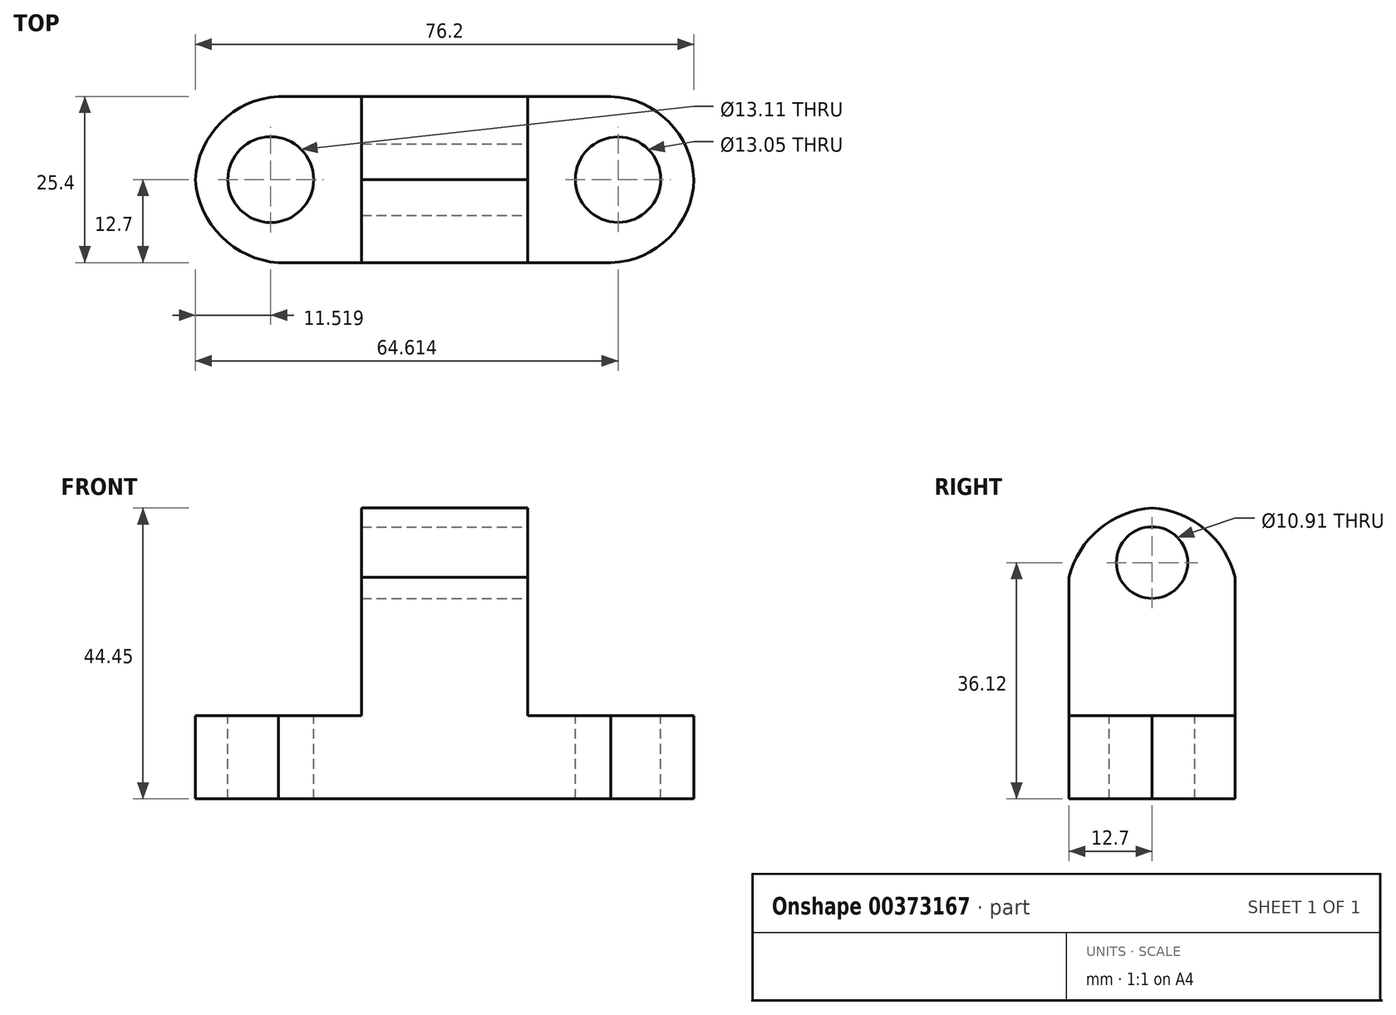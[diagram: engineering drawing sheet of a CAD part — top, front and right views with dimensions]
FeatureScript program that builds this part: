
annotation { "Feature Type Name" : "Feature", "Feature Type Description" : "" }
export const myFeature = defineFeature(function(context is Context, id is Id, definition is map)
    precondition{}
    {
        {
            var Q0;
            Q0=qCreatedBy(makeId("Front.planeOp"),FACE);
            var sketch = newSketch(context, id + "F0", { "sketchPlane" : qUnion([Q0])});
            skLineSegment(sketch, "E0", {"start": v(-13.94, 0) * mm, "end": v(-13.94, 12.7) * mm});
            skLineSegment(sketch, "E1", {"start": v(-13.94, 12.7) * mm, "end": v(11.46, 12.7) * mm});
            skLineSegment(sketch, "E2", {"start": v(11.46, 12.7) * mm, "end": v(11.46, 44.45) * mm});
            skLineSegment(sketch, "E3", {"start": v(11.46, 44.45) * mm, "end": v(36.86, 44.45) * mm});
            skLineSegment(sketch, "E4", {"start": v(36.86, 44.45) * mm, "end": v(36.86, 12.7) * mm});
            skLineSegment(sketch, "E5", {"start": v(36.86, 12.7) * mm, "end": v(62.26, 12.7) * mm});
            skLineSegment(sketch, "E6", {"start": v(62.26, 12.7) * mm, "end": v(62.26, 0) * mm});
            skLineSegment(sketch, "E7", {"start": v(62.26, 0) * mm, "end": v(-13.94, 0) * mm});
            skSolve(sketch);
        }
        {
            var Q0;
            Q0=makeQuery(id+"F0.imprint","IMPRINT",FACE,{"disambiguationData":[TD([[makeQuery(id+"F0.imprint","IMPRINT",EDGE,{"derivedFrom":sQuery(id+"F0.wireOp",EDGE,"E0")}),-1.0]])]});
            extrude(context, id + "F1", {"entities" : qUnion([Q0]), "depth" : 25.4 * mm});
        }
        {
            var Q0;
            Q0=makeQuery(id+"F1.opExtrude","SWEPT_FACE",FACE,{"disambiguationData":[OSD([sQuery(id+"F0.wireOp",EDGE,"E4")])]});
            var sketch = newSketch(context, id + "F2", { "sketchPlane" : qUnion([Q0])});
            skArc(sketch, "E8", {"start": v(-12.7, 44.45) * mm, "mid": v(-20.79, 41.23) * mm, "end": v(-25.4, 33.85) * mm});
            skArc(sketch, "E9", {"start": v(0, 33.85) * mm, "mid": v(-4.62, 41.22) * mm, "end": v(-12.7, 44.45) * mm});
            skSolve(sketch);
        }
        {
            var Q0;
            {var subQ0=sQuery(id+"F2.wireOp",EDGE,"E8");Q0=makeQuery(id+"F2.imprint","IMPRINT",FACE,{"disambiguationData":[TD([[makeQuery(id+"F2.imprint","IMPRINT",EDGE,{"derivedFrom":subQ0}),-1.0]])]});}
            var Q1;
            {var subQ0=sQuery(id+"F2.wireOp",EDGE,"E9");Q1=makeQuery(id+"F2.imprint","IMPRINT",FACE,{"disambiguationData":[TD([[makeQuery(id+"F2.imprint","IMPRINT",EDGE,{"derivedFrom":subQ0}),-1.0]])]});}
            extrude(context, id + "F3", {"entities" : qUnion([Q0, Q1]), "operationType" : NewBodyOperationType.REMOVE, "oppositeDirection" : true, "depth" : 25.4 * mm});
        }
        {
            var Q0;
            Q0=makeQuery(id+"F1.opExtrude","SWEPT_FACE",FACE,{"disambiguationData":[OSD([sQuery(id+"F0.wireOp",EDGE,"E4")])]});
            var sketch = newSketch(context, id + "F4", { "sketchPlane" : qUnion([Q0])});
            skCircle(sketch, "E10", {"center": v(-12.7, 36.12) * mm, "radius": 5.46 * mm});
            skSolve(sketch);
        }
        {
            var Q0;
            Q0=makeQuery(id+"F4.imprint","IMPRINT",FACE,{"disambiguationData":[TD([[makeQuery(id+"F4.imprint","IMPRINT",EDGE,{"derivedFrom":sQuery(id+"F4.wireOp",EDGE,"E10")}),1.0]])]});
            extrude(context, id + "F5", {"entities" : qUnion([Q0]), "operationType" : NewBodyOperationType.REMOVE, "oppositeDirection" : true, "depth" : 25.4 * mm});
        }
        {
            var Q0;
            Q0=makeQuery(id+"F1.opExtrude","SWEPT_FACE",FACE,{"disambiguationData":[OSD([sQuery(id+"F0.wireOp",EDGE,"E1")])]});
            var sketch = newSketch(context, id + "F6", { "sketchPlane" : qUnion([Q0])});
            skArc(sketch, "E11", {"start": v(-13.94, -12.7) * mm, "mid": v(-9.97, -21.43) * mm, "end": v(-1.24, -25.4) * mm});
            skArc(sketch, "E12", {"start": v(-1.24, 0) * mm, "mid": v(-10.02, -3.93) * mm, "end": v(-13.94, -12.7) * mm});
            skCircle(sketch, "E13", {"center": v(-2.42, -12.7) * mm, "radius": 6.56 * mm});
            skSolve(sketch);
        }
        {
            var Q0;
            {var subQ0=sQuery(id+"F6.wireOp",EDGE,"E12");Q0=makeQuery(id+"F6.imprint","IMPRINT",FACE,{"disambiguationData":[TD([[makeQuery(id+"F6.imprint","IMPRINT",EDGE,{"derivedFrom":subQ0}),-1.0]])]});}
            var Q1;
            {var subQ0=sQuery(id+"F6.wireOp",EDGE,"E11");Q1=makeQuery(id+"F6.imprint","IMPRINT",FACE,{"disambiguationData":[TD([[makeQuery(id+"F6.imprint","IMPRINT",EDGE,{"derivedFrom":subQ0}),-1.0]])]});}
            var Q2;
            Q2=makeQuery(id+"F6.imprint","IMPRINT",FACE,{"disambiguationData":[TD([[makeQuery(id+"F6.imprint","IMPRINT",EDGE,{"derivedFrom":sQuery(id+"F6.wireOp",EDGE,"E13")}),1.0]])]});
            extrude(context, id + "F7", {"entities" : qUnion([Q0, Q1, Q2]), "operationType" : NewBodyOperationType.REMOVE, "oppositeDirection" : true, "depth" : 12.7 * mm});
        }
        {
            var Q0;
            Q0=makeQuery(id+"F1.opExtrude","SWEPT_FACE",FACE,{"disambiguationData":[OSD([sQuery(id+"F0.wireOp",EDGE,"E5")])]});
            var sketch = newSketch(context, id + "F8", { "sketchPlane" : qUnion([Q0])});
            skArc(sketch, "E14", {"start": v(62.26, -12.7) * mm, "mid": v(58.4, -3.85) * mm, "end": v(49.56, 0) * mm});
            skArc(sketch, "E15", {"start": v(49.56, -25.4) * mm, "mid": v(58.44, -21.58) * mm, "end": v(62.26, -12.7) * mm});
            skCircle(sketch, "E16", {"center": v(50.67, -12.7) * mm, "radius": 6.53 * mm});
            skSolve(sketch);
        }
        {
            var Q0;
            Q0=makeQuery(id+"F8.imprint","IMPRINT",FACE,{"disambiguationData":[TD([[makeQuery(id+"F8.imprint","IMPRINT",EDGE,{"derivedFrom":sQuery(id+"F8.wireOp",EDGE,"E16")}),1.0]])]});
            var Q1;
            {var subQ0=sQuery(id+"F8.wireOp",EDGE,"E14");Q1=makeQuery(id+"F8.imprint","IMPRINT",FACE,{"disambiguationData":[TD([[makeQuery(id+"F8.imprint","IMPRINT",EDGE,{"derivedFrom":subQ0}),-1.0]])]});}
            var Q2;
            {var subQ0=sQuery(id+"F8.wireOp",EDGE,"E15");Q2=makeQuery(id+"F8.imprint","IMPRINT",FACE,{"disambiguationData":[TD([[makeQuery(id+"F8.imprint","IMPRINT",EDGE,{"derivedFrom":subQ0}),-1.0]])]});}
            extrude(context, id + "F9", {"entities" : qUnion([Q0, Q1, Q2]), "operationType" : NewBodyOperationType.REMOVE, "oppositeDirection" : true, "depth" : 25.4 * mm});
        }
    });
